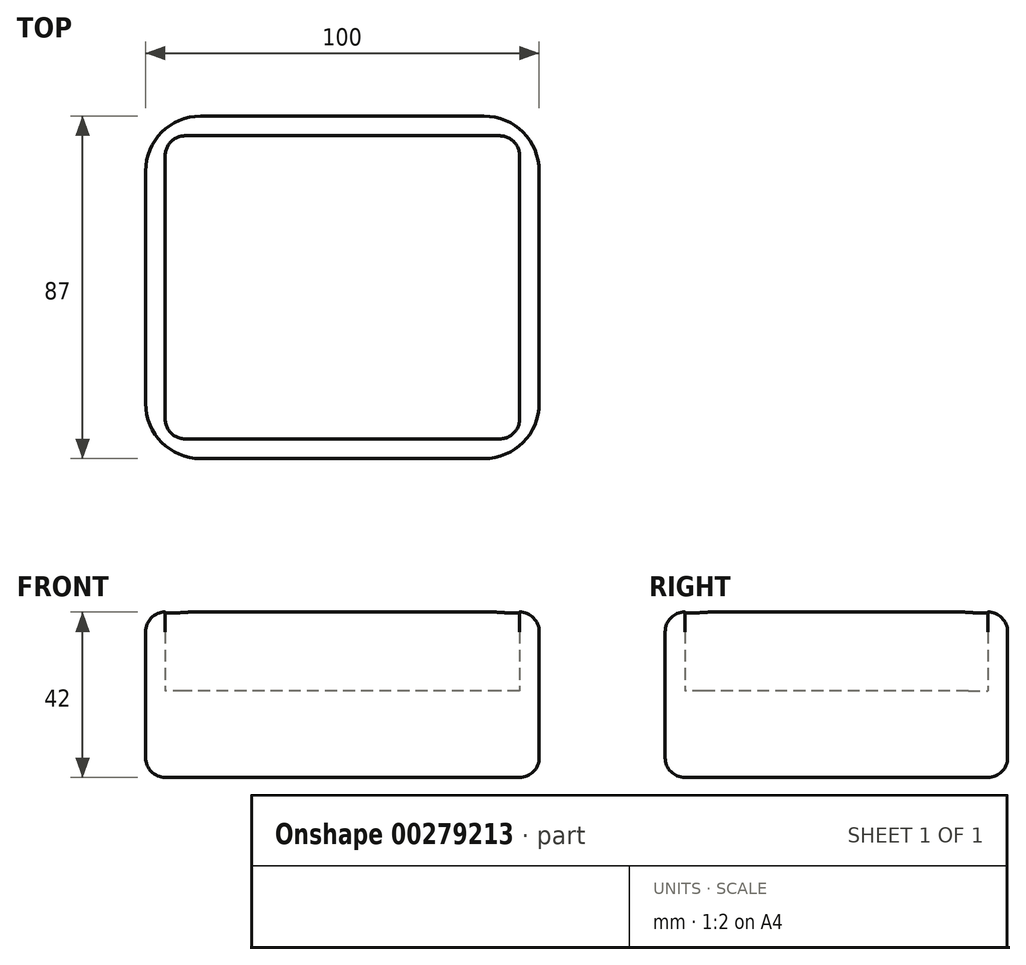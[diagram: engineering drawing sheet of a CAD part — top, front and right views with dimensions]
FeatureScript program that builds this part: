
annotation { "Feature Type Name" : "Feature", "Feature Type Description" : "" }
export const myFeature = defineFeature(function(context is Context, id is Id, definition is map)
    precondition{}
    {
        {
            var Q0;
            Q0=qCreatedBy(makeId("Top.planeOp"),FACE);
            var sketch = newSketch(context, id + "F0", { "sketchPlane" : qUnion([Q0])});
            skLineSegment(sketch, "E0.bottom", {"start": v(45, 38.5) * mm, "end": v(-45, 38.5) * mm});
            skLineSegment(sketch, "E0.top", {"start": v(45, -38.5) * mm, "end": v(-45, -38.5) * mm});
            skLineSegment(sketch, "E0.left", {"start": v(45, 38.5) * mm, "end": v(45, -38.5) * mm});
            skLineSegment(sketch, "E0.right", {"start": v(-45, 38.5) * mm, "end": v(-45, -38.5) * mm});
            skPoint(sketch, "E0.middle", {"position": v(0, 0) * mm});
            skLineSegment(sketch, "E1.bottom", {"start": v(50, 43.5) * mm, "end": v(-50, 43.5) * mm});
            skLineSegment(sketch, "E1.top", {"start": v(50, -43.5) * mm, "end": v(-50, -43.5) * mm});
            skLineSegment(sketch, "E1.left", {"start": v(50, 43.5) * mm, "end": v(50, -43.5) * mm});
            skLineSegment(sketch, "E1.right", {"start": v(-50, 43.5) * mm, "end": v(-50, -43.5) * mm});
            skSolve(sketch);
        }
        {
            var Q0;
            Q0=makeQuery(id+"F0.imprint","IMPRINT",FACE,{"disambiguationData":[TD([[makeQuery(id+"F0.imprint","IMPRINT",EDGE,{"derivedFrom":sQuery(id+"F0.wireOp",EDGE,"E0.bottom")}),1.0]])]});
            extrude(context, id + "F1", {"entities" : qUnion([Q0]), "depth" : 22 * mm});
        }
        {
            var Q0;
            Q0 = qSketchRegion(id + "F0", true);
            extrude(context, id + "F2", {"entities" : qUnion([Q0]), "operationType" : NewBodyOperationType.ADD, "depth" : 42 * mm});
        }
        {
            var Q0;
            Q0=makeQuery(id+"F2.opExtrude","SWEPT_EDGE",EDGE,{"disambiguationData":[OSD([sQuery(id+"F0.wireOp",EDGE,"E1.top"),sQuery(id+"F0.wireOp",EDGE,"E1.right")])]});
            var Q1;
            Q1=makeQuery(id+"F2.opExtrude","SWEPT_EDGE",EDGE,{"disambiguationData":[OSD([sQuery(id+"F0.wireOp",EDGE,"E1.bottom"),sQuery(id+"F0.wireOp",EDGE,"E1.right")])]});
            var Q2;
            Q2=makeQuery(id+"F2.opExtrude","SWEPT_EDGE",EDGE,{"disambiguationData":[OSD([sQuery(id+"F0.wireOp",EDGE,"E1.bottom"),sQuery(id+"F0.wireOp",EDGE,"E1.left")])]});
            var Q3;
            Q3=makeQuery(id+"F2.opExtrude","SWEPT_EDGE",EDGE,{"disambiguationData":[OSD([sQuery(id+"F0.wireOp",EDGE,"E1.top"),sQuery(id+"F0.wireOp",EDGE,"E1.left")])]});
            fillet(context, id + "F3", {"entities" : qUnion([Q0, Q1, Q2, Q3]), "radius" : 14 * mm, "tangentPropagation" : true, "allowEdgeOverflow" : false});
        }
        {
            var Q0;
            Q0=makeQuery(id+"F2.opExtrude","CAP_EDGE",EDGE,{"disambiguationData":[OSD([sQuery(id+"F0.wireOp",EDGE,"E1.bottom")])],"isStart":true});
            fillet(context, id + "F4", {"entities" : qUnion([Q0]), "radius" : 5 * mm, "tangentPropagation" : true, "allowEdgeOverflow" : false});
        }
        {
            var Q0;
            Q0=makeQuery(id+"F2.opExtrude","SWEPT_EDGE",EDGE,{"disambiguationData":[OSD([sQuery(id+"F0.wireOp",EDGE,"E0.top"),sQuery(id+"F0.wireOp",EDGE,"E0.right")])]});
            var Q1;
            Q1=makeQuery(id+"F2.opExtrude","SWEPT_EDGE",EDGE,{"disambiguationData":[OSD([sQuery(id+"F0.wireOp",EDGE,"E0.top"),sQuery(id+"F0.wireOp",EDGE,"E0.left")])]});
            var Q2;
            Q2=makeQuery(id+"F2.opExtrude","SWEPT_EDGE",EDGE,{"disambiguationData":[OSD([sQuery(id+"F0.wireOp",EDGE,"E0.bottom"),sQuery(id+"F0.wireOp",EDGE,"E0.right")])]});
            var Q3;
            Q3=makeQuery(id+"F2.opExtrude","SWEPT_EDGE",EDGE,{"disambiguationData":[OSD([sQuery(id+"F0.wireOp",EDGE,"E0.bottom"),sQuery(id+"F0.wireOp",EDGE,"E0.left")])]});
            fillet(context, id + "F5", {"entities" : qUnion([Q0, Q1, Q2, Q3]), "radius" : 5 * mm, "tangentPropagation" : true, "allowEdgeOverflow" : false});
        }
        {
            var Q0;
            Q0=makeQuery(id+"F2.opExtrude","CAP_EDGE",EDGE,{"disambiguationData":[OSD([sQuery(id+"F0.wireOp",EDGE,"E1.top")])],"isStart":false});
            fillet(context, id + "F6", {"entities" : qUnion([Q0]), "radius" : 5 * mm, "tangentPropagation" : true, "allowEdgeOverflow" : false});
        }
    });
